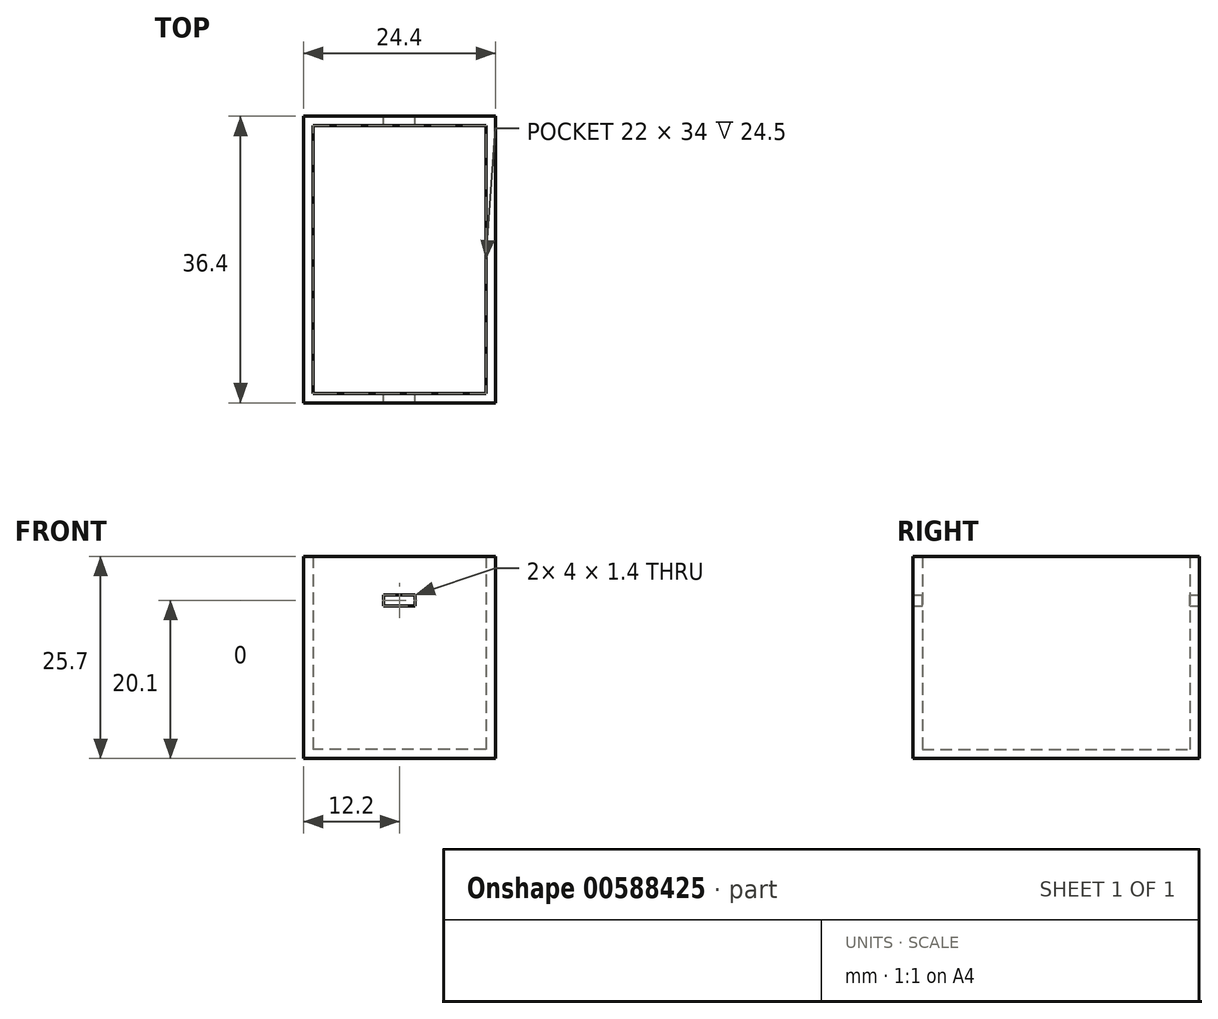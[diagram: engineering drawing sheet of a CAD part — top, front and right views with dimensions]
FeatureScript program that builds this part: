
annotation { "Feature Type Name" : "Feature", "Feature Type Description" : "" }
export const myFeature = defineFeature(function(context is Context, id is Id, definition is map)
    precondition{}
    {
        {
            var Q0;
            Q0=qCreatedBy(makeId("Top.planeOp"),FACE);
            var sketch = newSketch(context, id + "F0", { "sketchPlane" : qUnion([Q0])});
            skLineSegment(sketch, "E0.bottom", {"start": v(11, -17) * mm, "end": v(-11, -17) * mm});
            skLineSegment(sketch, "E0.top", {"start": v(11, 17) * mm, "end": v(-11, 17) * mm});
            skLineSegment(sketch, "E0.left", {"start": v(11, -17) * mm, "end": v(11, 17) * mm});
            skLineSegment(sketch, "E0.right", {"start": v(-11, -17) * mm, "end": v(-11, 17) * mm});
            skPoint(sketch, "E0.middle", {"position": v(0, 0) * mm});
            skLineSegment(sketch, "E1.0", {"start": v(12.2, 18.2) * mm, "end": v(-12.2, 18.2) * mm});
            skLineSegment(sketch, "E1.1", {"start": v(12.2, -18.2) * mm, "end": v(12.2, 18.2) * mm});
            skLineSegment(sketch, "E1.2", {"start": v(12.2, -18.2) * mm, "end": v(-12.2, -18.2) * mm});
            skLineSegment(sketch, "E1.3", {"start": v(-12.2, -18.2) * mm, "end": v(-12.2, 18.2) * mm});
            skSolve(sketch);
        }
        {
            var Q0;
            Q0=makeQuery(id+"F0.imprint","IMPRINT",FACE,{"disambiguationData":[TD([[makeQuery(id+"F0.imprint","IMPRINT",EDGE,{"derivedFrom":sQuery(id+"F0.wireOp",EDGE,"E0.bottom")}),-1.0]])]});
            extrude(context, id + "F1", {"entities" : qUnion([Q0]), "depth" : 1.2 * mm, "offsetDistance" : 25 * mm});
        }
        {
            var Q0;
            Q0 = qSketchRegion(id + "F0", true);
            extrude(context, id + "F2", {"entities" : qUnion([Q0]), "operationType" : NewBodyOperationType.ADD, "depth" : 25.7 * mm, "offsetDistance" : 25 * mm});
        }
        {
            var Q0;
            Q0=makeQuery(id+"F2.opExtrude","SWEPT_FACE",FACE,{"disambiguationData":[OSD([sQuery(id+"F0.wireOp",EDGE,"E1.0")])]});
            var sketch = newSketch(context, id + "F3", { "sketchPlane" : qUnion([Q0])});
            skLineSegment(sketch, "E2.bottom", {"start": v(-2, 20.8) * mm, "end": v(2, 20.8) * mm});
            skLineSegment(sketch, "E2.top", {"start": v(-2, 19.4) * mm, "end": v(2, 19.4) * mm});
            skLineSegment(sketch, "E2.left", {"start": v(-2, 20.8) * mm, "end": v(-2, 19.4) * mm});
            skLineSegment(sketch, "E2.right", {"start": v(2, 20.8) * mm, "end": v(2, 19.4) * mm});
            skSolve(sketch);
        }
        {
            var Q0;
            Q0=makeQuery(id+"F3.imprint","IMPRINT",FACE,{"disambiguationData":[TD([[makeQuery(id+"F3.imprint","IMPRINT",EDGE,{"derivedFrom":sQuery(id+"F3.wireOp",EDGE,"E2.bottom")}),-1.0]])]});
            extrude(context, id + "F4", {"entities" : qUnion([Q0]), "operationType" : NewBodyOperationType.REMOVE, "endBound" : BoundingType.THROUGH_ALL, "oppositeDirection" : true, "depth" : 25 * mm, "offsetDistance" : 25 * mm});
        }
    });
